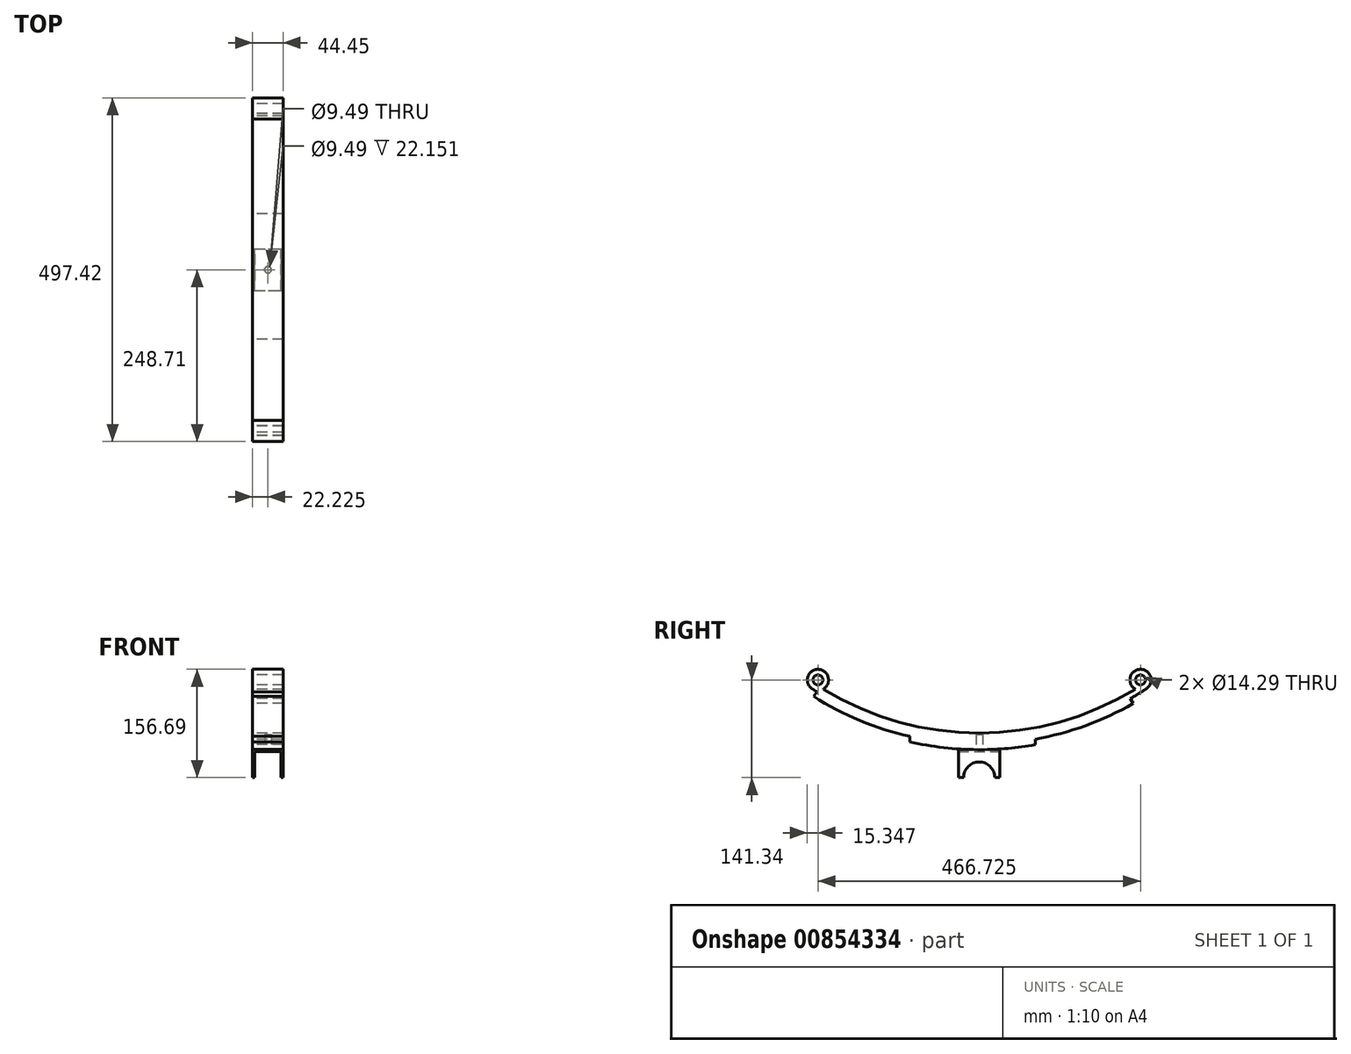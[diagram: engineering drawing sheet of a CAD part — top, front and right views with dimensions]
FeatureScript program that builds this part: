
annotation { "Feature Type Name" : "Feature", "Feature Type Description" : "" }
export const myFeature = defineFeature(function(context is Context, id is Id, definition is map)
    precondition{}
    {
        {
            var Q0;
            Q0=qCreatedBy(makeId("Right.planeOp"),FACE);
            var sketch = newSketch(context, id + "F0", { "sketchPlane" : qUnion([Q0])});
            skCircle(sketch, "E0", {"center": v(-233.36, 0) * mm, "radius": 7.14 * mm});
            skCircle(sketch, "E1", {"center": v(233.36, 0) * mm, "radius": 7.14 * mm});
            skLineSegment(sketch, "E2", {"start": v(-233.36, 0) * mm, "end": v(233.36, 0) * mm, "construction": true});
            skArc(sketch, "E3", {"start": v(-225.71, -13.3) * mm, "mid": v(0, -76.9) * mm, "end": v(225.71, -13.3) * mm});
            skArc(sketch, "E4.0", {"start": v(-241.78, -12.83) * mm, "mid": v(-238.37, -15.05) * mm, "end": v(-234.93, -17.24) * mm});
            skArc(sketch, "E5.0", {"start": v(-225.71, -13.3) * mm, "mid": v(-232.9, 15.34) * mm, "end": v(-241.78, -12.83) * mm});
            skArc(sketch, "E6.0", {"start": v(241.78, -12.83) * mm, "mid": v(232.9, 15.34) * mm, "end": v(225.71, -13.3) * mm});
            skArc(sketch, "E7.0", {"start": v(-239.77, -23.89) * mm, "mid": v(-172.67, -58.76) * mm, "end": v(-100.66, -81.87) * mm});
            skLineSegment(sketch, "E8", {"start": v(-234.93, -17.24) * mm, "end": v(-239.77, -23.89) * mm});
            skLineSegment(sketch, "E9", {"start": v(0, -114.47) * mm, "end": v(0, 0) * mm, "construction": true});
            skArc(sketch, "E10.trimOffspring", {"start": v(218.4, -27.16) * mm, "mid": v(230.2, -20.18) * mm, "end": v(241.78, -12.83) * mm});
            skLineSegment(sketch, "E11.MirrorCS", {"start": v(-399.64, 176.46) * mm, "end": v(-290.7, 211.63) * mm, "construction": true});
            skLineSegment(sketch, "E12", {"start": v(218.4, -27.16) * mm, "end": v(222.75, -34.12) * mm});
            skLineSegment(sketch, "E13", {"start": v(-100.66, -81.87) * mm, "end": v(-100.66, -89.7) * mm});
            skLineSegment(sketch, "E14", {"start": v(80.95, -85.94) * mm, "end": v(81.1, -93.84) * mm});
            skArc(sketch, "E15.trimOffspring", {"start": v(-100.66, -89.7) * mm, "mid": v(-51.64, -98.04) * mm, "end": v(-2, -101) * mm});
            skArc(sketch, "E16.trimOffspring", {"start": v(80.95, -85.94) * mm, "mid": v(154.05, -66.04) * mm, "end": v(222.75, -34.12) * mm});
            skLineSegment(sketch, "E17", {"start": v(2, -101.01) * mm, "end": v(-2, -101) * mm});
            skArc(sketch, "E18.trimOffspring", {"start": v(2, -101.01) * mm, "mid": v(41.7, -99.15) * mm, "end": v(81.1, -93.84) * mm});
            skSolve(sketch);
        }
        {
            var Q0;
            Q0=makeQuery(id+"F0.imprint","IMPRINT",FACE,{"disambiguationData":[TD([[makeQuery(id+"F0.imprint","IMPRINT",EDGE,{"derivedFrom":sQuery(id+"F0.wireOp",EDGE,"E0")}),-1.0]])]});
            extrude(context, id + "F1", {"entities" : qUnion([Q0]), "depth" : 44.45 * mm, "offsetDistance" : 25 * mm});
        }
        {
            var Q0;
            Q0=qCreatedBy(makeId("Front.planeOp"),FACE);
            var sketch = newSketch(context, id + "F2", { "sketchPlane" : qUnion([Q0])});
            skLineSegment(sketch, "E19.bottom", {"start": v(0, -100.69) * mm, "end": v(44.43, -100.69) * mm});
            skLineSegment(sketch, "E19.left", {"start": v(0, -100.69) * mm, "end": v(0, -141.34) * mm});
            skLineSegment(sketch, "E19.right", {"start": v(44.43, -100.69) * mm, "end": v(44.43, -141.34) * mm});
            skLineSegment(sketch, "E20.0", {"start": v(41.26, -103.86) * mm, "end": v(41.26, -141.34) * mm});
            skLineSegment(sketch, "E20.1", {"start": v(3.17, -103.86) * mm, "end": v(41.26, -103.86) * mm});
            skLineSegment(sketch, "E20.2", {"start": v(3.17, -103.86) * mm, "end": v(3.17, -141.34) * mm});
            skLineSegment(sketch, "E21", {"start": v(0, -141.34) * mm, "end": v(3.17, -141.34) * mm});
            skLineSegment(sketch, "E22", {"start": v(41.26, -141.34) * mm, "end": v(44.43, -141.34) * mm});
            skSolve(sketch);
        }
        {
            var Q0;
            Q0=makeQuery(id+"F2.imprint","IMPRINT",FACE,{"disambiguationData":[TD([[makeQuery(id+"F2.imprint","IMPRINT",EDGE,{"derivedFrom":sQuery(id+"F2.wireOp",EDGE,"E19.bottom")}),-1.0]])]});
            extrude(context, id + "F3", {"entities" : qUnion([Q0]), "endBound" : BoundingType.SYMMETRIC, "depth" : 60 * mm, "offsetDistance" : 25 * mm});
        }
        {
            var Q0;
            Q0=makeQuery(id+"F3.opExtrude","SWEPT_FACE",FACE,{"disambiguationData":[OSD([sQuery(id+"F2.wireOp",EDGE,"E19.left")])]});
            var sketch = newSketch(context, id + "F4", { "sketchPlane" : qUnion([Q0])});
            skArc(sketch, "E23", {"start": v(22.5, -141.34) * mm, "mid": v(0, -118.84) * mm, "end": v(-22.5, -141.34) * mm});
            skLineSegment(sketch, "E24", {"start": v(0, 0) * mm, "end": v(0, -163.99) * mm, "construction": true});
            skLineSegment(sketch, "E25", {"start": v(-22.5, -141.34) * mm, "end": v(22.5, -141.34) * mm});
            skSolve(sketch);
        }
        {
            var Q0;
            Q0 = qSketchRegion(id + "F4", true);
            extrude(context, id + "F5", {"entities" : qUnion([Q0]), "operationType" : NewBodyOperationType.REMOVE, "endBound" : BoundingType.THROUGH_ALL, "oppositeDirection" : true, "depth" : 25 * mm, "offsetDistance" : 25 * mm});
        }
        {
            var Q0;
            Q0=makeQuery(id+"F3.opExtrude","SWEPT_FACE",FACE,{"disambiguationData":[OSD([sQuery(id+"F2.wireOp",EDGE,"E20.1")])]});
            var sketch = newSketch(context, id + "F6", { "sketchPlane" : qUnion([Q0])});
            skLineSegment(sketch, "E26", {"start": v(22.22, -30) * mm, "end": v(22.22, 30) * mm, "construction": true});
            skLineSegment(sketch, "E27", {"start": v(0, 0) * mm, "end": v(44.45, 0) * mm, "construction": true});
            skCircle(sketch, "E28", {"center": v(22.22, 0) * mm, "radius": 4.74 * mm});
            skSolve(sketch);
        }
        {
            var Q0;
            Q0=makeQuery(id+"F6.imprint","IMPRINT",FACE,{"disambiguationData":[TD([[makeQuery(id+"F6.imprint","IMPRINT",EDGE,{"derivedFrom":sQuery(id+"F6.wireOp",EDGE,"E28")}),1.0]])]});
            extrude(context, id + "F7", {"entities" : qUnion([Q0]), "operationType" : NewBodyOperationType.REMOVE, "oppositeDirection" : true, "depth" : 25 * mm, "offsetDistance" : 25 * mm});
        }
    });
